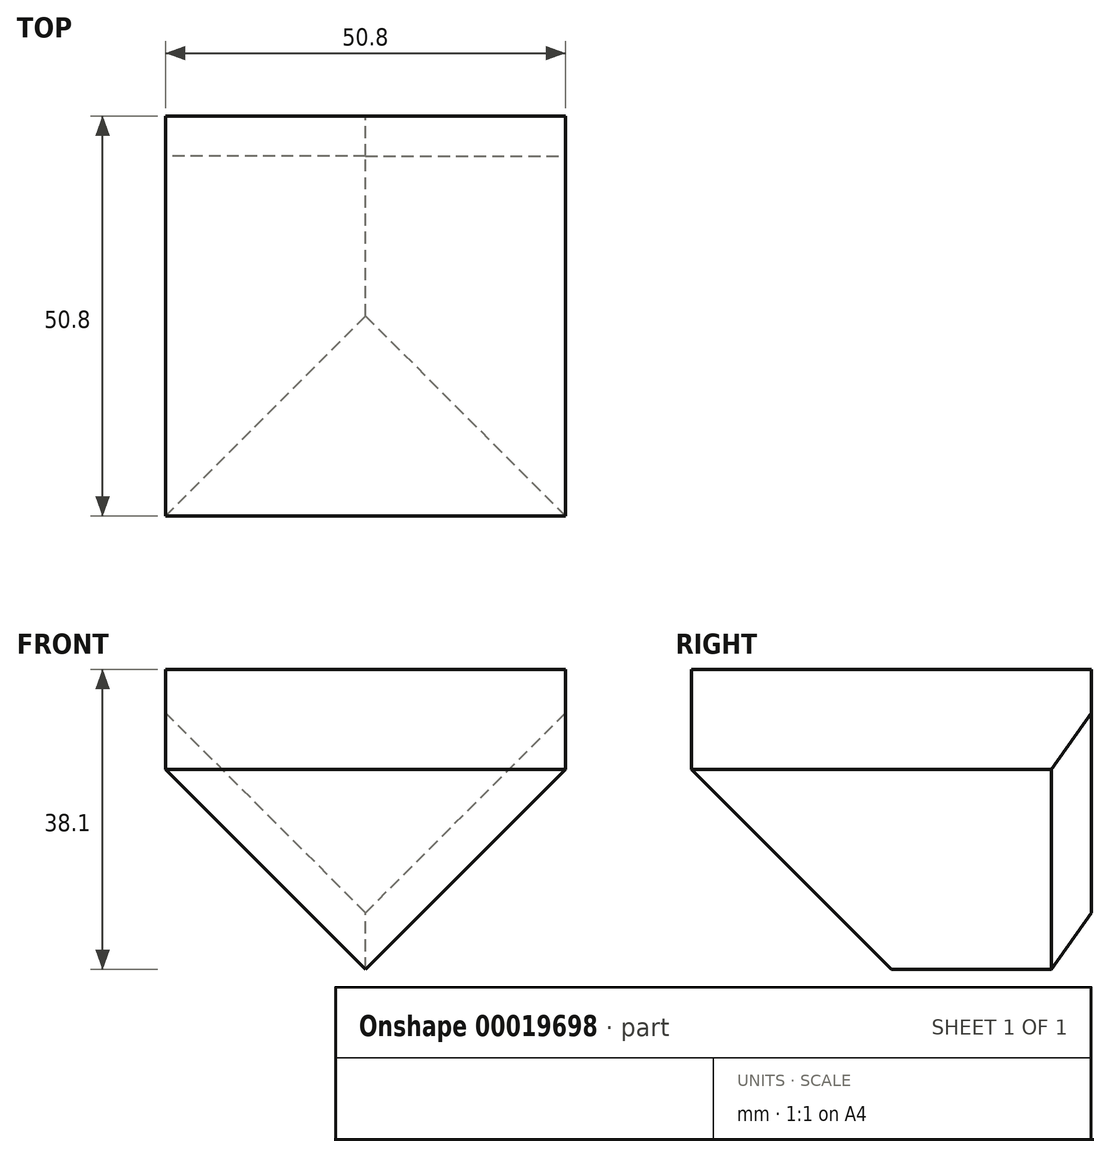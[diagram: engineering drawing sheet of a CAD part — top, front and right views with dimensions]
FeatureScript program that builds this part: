
annotation { "Feature Type Name" : "Feature", "Feature Type Description" : "" }
export const myFeature = defineFeature(function(context is Context, id is Id, definition is map)
    precondition{}
    {
        {
            var Q0;
            Q0=qCreatedBy(makeId("Front.planeOp"),FACE);
            var sketch = newSketch(context, id + "F0", { "sketchPlane" : qUnion([Q0])});
            skLineSegment(sketch, "E0.bottom", {"start": v(-38.95, 39.61) * mm, "end": v(11.85, 39.61) * mm});
            skLineSegment(sketch, "E0.top", {"start": v(-38.95, -11.19) * mm, "end": v(11.85, -11.19) * mm});
            skLineSegment(sketch, "E0.left", {"start": v(-38.95, 39.61) * mm, "end": v(-38.95, -11.19) * mm});
            skLineSegment(sketch, "E0.right", {"start": v(11.85, 39.61) * mm, "end": v(11.85, -11.19) * mm});
            skSolve(sketch);
        }
        {
            var Q0;
            Q0=makeQuery(id+"F0.imprint","IMPRINT",FACE,{"disambiguationData":[TD([[makeQuery(id+"F0.imprint","IMPRINT",EDGE,{"derivedFrom":sQuery(id+"F0.wireOp",EDGE,"E0.bottom")}),-1.0]])]});
            extrude(context, id + "F1", {"entities" : qUnion([Q0]), "depth" : 50.8 * mm});
        }
        {
            var Q0;
            Q0=makeQuery(id+"F1.opExtrude","SWEPT_EDGE",EDGE,{"disambiguationData":[OSD([sQuery(id+"F0.wireOp",EDGE,"E0.top"),sQuery(id+"F0.wireOp",EDGE,"E0.left")])]});
            var Q1;
            Q1=makeQuery(id+"F1.opExtrude","CAP_EDGE",EDGE,{"disambiguationData":[OSD([sQuery(id+"F0.wireOp",EDGE,"E0.top")])],"isStart":false});
            chamfer(context, id + "F2", {"entities" : qUnion([Q0, Q1]), "width" : 38.1 * mm, "tangentPropagation" : true});
        }
        {
            var Q0;
            Q0=makeQuery(id+"F1.opExtrude","SWEPT_EDGE",EDGE,{"disambiguationData":[OSD([sQuery(id+"F0.wireOp",EDGE,"E0.top"),sQuery(id+"F0.wireOp",EDGE,"E0.right")])]});
            chamfer(context, id + "F3", {"entities" : qUnion([Q0]), "width" : 38.1 * mm, "tangentPropagation" : true});
        }
        {
            var Q0;
            {var subQ0=sQuery(id+"F0.wireOp",EDGE,"E0.top");var subQ1=sQuery(id+"F0.wireOp",EDGE,"E0.right");Q0=makeQuery(id+"F3.opChamfer","BLEND_EDGE",EDGE,{"blendedFrom":[makeQuery(id+"F1.opExtrude","SWEPT_EDGE",EDGE,{"disambiguationData":[OSD([subQ0,subQ1])]}),makeQuery(id+"F1.opExtrude","CAP_FACE",FACE,{"disambiguationData":[OSD([sQuery(id+"F0.wireOp",EDGE,"E0.bottom"),subQ0,sQuery(id+"F0.wireOp",EDGE,"E0.left"),subQ1])],"isStart":true})],"blendedInto":[makeQuery(id+"F1.opExtrude","CAP_FACE",FACE,{"disambiguationData":[OSD([sQuery(id+"F0.wireOp",EDGE,"E0.bottom"),subQ0,sQuery(id+"F0.wireOp",EDGE,"E0.left"),subQ1])],"isStart":true})]});}
            var Q1;
            {var subQ0=sQuery(id+"F0.wireOp",EDGE,"E0.top");var subQ1=sQuery(id+"F0.wireOp",EDGE,"E0.left");Q1=makeQuery(id+"F2.opChamfer","BLEND_EDGE",EDGE,{"blendedFrom":[makeQuery(id+"F1.opExtrude","SWEPT_EDGE",EDGE,{"disambiguationData":[OSD([subQ0,subQ1])]}),makeQuery(id+"F1.opExtrude","CAP_FACE",FACE,{"disambiguationData":[OSD([sQuery(id+"F0.wireOp",EDGE,"E0.bottom"),subQ0,subQ1,sQuery(id+"F0.wireOp",EDGE,"E0.right")])],"isStart":true})],"blendedInto":[makeQuery(id+"F1.opExtrude","CAP_FACE",FACE,{"disambiguationData":[OSD([sQuery(id+"F0.wireOp",EDGE,"E0.bottom"),subQ0,subQ1,sQuery(id+"F0.wireOp",EDGE,"E0.right")])],"isStart":true})]});}
            chamfer(context, id + "F4", {"entities" : qUnion([Q0, Q1]), "width" : 5.08 * mm, "tangentPropagation" : true});
        }
    });
